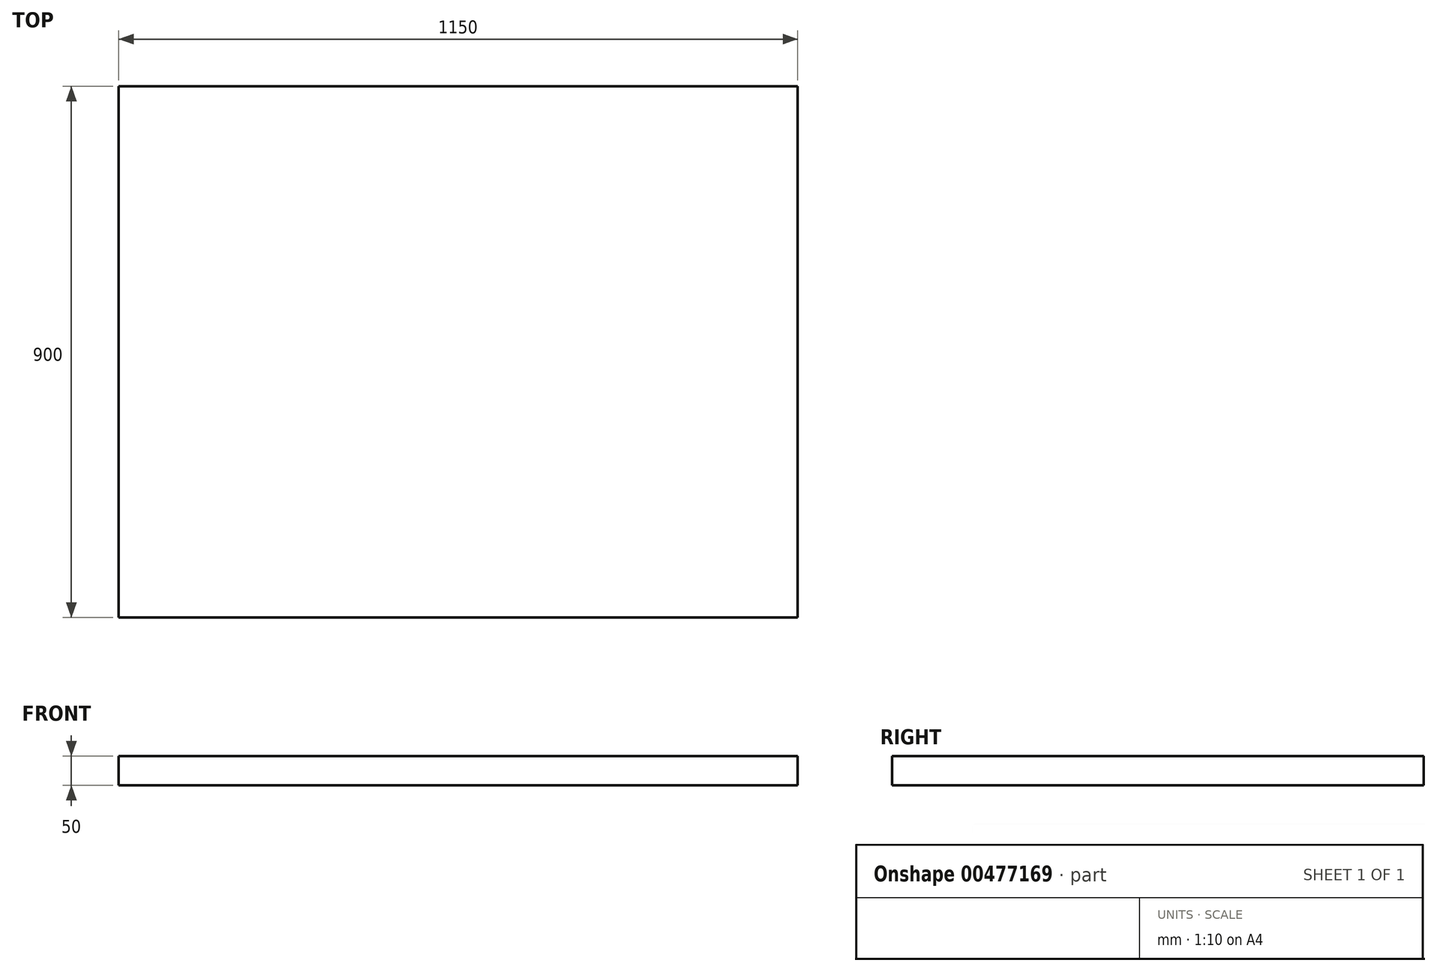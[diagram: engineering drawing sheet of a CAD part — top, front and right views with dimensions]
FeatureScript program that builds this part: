
annotation { "Feature Type Name" : "Feature", "Feature Type Description" : "" }
export const myFeature = defineFeature(function(context is Context, id is Id, definition is map)
    precondition{}
    {
        {
            var Q0;
            Q0=qCreatedBy(makeId("Top.planeOp"),FACE);
            var sketch = newSketch(context, id + "F0", { "sketchPlane" : qUnion([Q0])});
            skLineSegment(sketch, "E0.bottom", {"start": v(575, -450) * mm, "end": v(-575, -450) * mm});
            skLineSegment(sketch, "E0.top", {"start": v(575, 450) * mm, "end": v(-575, 450) * mm});
            skLineSegment(sketch, "E0.left", {"start": v(575, -450) * mm, "end": v(575, 450) * mm});
            skLineSegment(sketch, "E0.right", {"start": v(-575, -450) * mm, "end": v(-575, 450) * mm});
            skPoint(sketch, "E0.middle", {"position": v(0, 0) * mm});
            skSolve(sketch);
        }
        {
            var Q0;
            Q0=makeQuery(id+"F0.imprint","IMPRINT",FACE,{"disambiguationData":[TD([[makeQuery(id+"F0.imprint","IMPRINT",EDGE,{"derivedFrom":sQuery(id+"F0.wireOp",EDGE,"E0.bottom")}),-1.0]])]});
            extrude(context, id + "F1", {"entities" : qUnion([Q0]), "depth" : 50 * mm});
        }
    });
